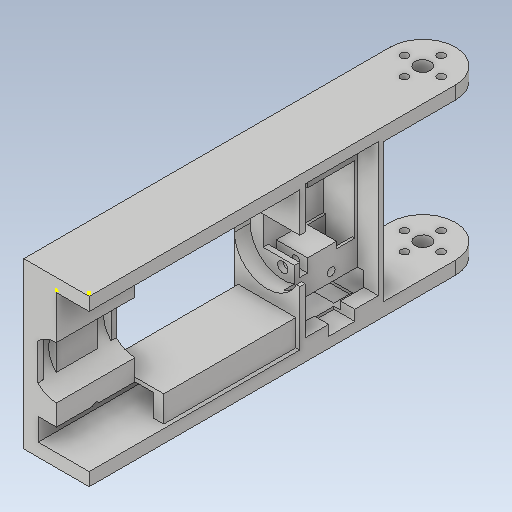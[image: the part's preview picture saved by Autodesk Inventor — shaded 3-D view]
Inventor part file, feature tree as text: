
AUTODESK INVENTOR PART (.ipt)
format: ipt  version: 2020.1 (Build 241239000, 239)  size: 703,488 bytes
history: native  units: mm
features: sketch x34, extrude x33, other x30, mirror x2
ambient origin geometry x8: Origin, YZ Plane, XZ Plane, XY Plane, X Axis, Y Axis, Z Axis, Center Point
bodies: Body1 (feature_tree), Body2 (feature_tree)
feature tree (99):
  other  "Sólido1"
  extrude  "Extrusión1"  Depth=25.0mm
  sketch  "Boceto2"  dims[d2=6.0mm d7=3.0mm]
  extrude  "Extrusión2"  Depth=3.0mm
  extrude  "Extrusión3"  Depth=5.0mm TaperAngle=0.0deg
  sketch  "Boceto5"  dims[d13=12.5mm d14=0.0mm d15=5.0mm d16=0.0mm]
  extrude  "Extrusión4"  Depth=33.0mm
  extrude  "Extrusión6"  Depth=5.0mm TaperAngle=0.0deg
  extrude  "Extrusión7"  Depth=7.0mm
  mirror  "Simetría1"
  mirror  "Simetría2"
  extrude  "Extrusión8"  Depth=2.0mm TaperAngle=0.0deg
  other  "Edición directa1"
  other  "Edición directa2"
  other  "Edición directa3"
  other  "Edición directa4"
  extrude  "Extrusión9"  Depth=2.0mm TaperAngle=0.0deg
  other  "Edición directa5"
  extrude  "Extrusión10"  Depth=0.5mm TaperAngle=0.0deg
  extrude  "Extrusión11"  TaperAngle=0.0deg  [1 undecoded]
  extrude  "Extrusión12"  Depth=28.0mm
  extrude  "Extrusión13"  Depth=4.0mm TaperAngle=0.0deg
  extrude  "Extrusión14"  Depth=8.0mm
  extrude  "Extrusión15"  Depth=3.0mm
  extrude  "Extrusión16"  Depth=18.0mm
  extrude  "Extrusión17"  Depth=3.0mm
  extrude  "Extrusión18"  Depth=7.5mm
  extrude  "Extrusión19"  Depth=7.0mm
  other  "Edición directa6"
  extrude  "Extrusión20"  Depth=3.5mm
  extrude  "Extrusión21"  Depth=27.0mm
  extrude  "Extrusión22"  Depth=0.5mm
  extrude  "Extrusión23"  Depth=25.0mm TaperAngle=0.0deg
  other  "Edición directa7"
  extrude  "Extrusión24"  Depth=5.0mm
  extrude  "Extrusión25"  TaperAngle=0.0deg  [1 undecoded]
  extrude  "Extrusión26"  Depth=2.0mm
  extrude  "Extrusión27"  TaperAngle=270.0deg  [1 undecoded]
  extrude  "Extrusión28"  Depth=2.0mm TaperAngle=0.0deg
  extrude  "Extrusión29"  Depth=9.0mm
  other  "Edición directa8"
  extrude  "Extrusión30"  Depth=5.5mm
  other  "Edición directa9"
  other  "Edición directa10"
  other  "Edición directa11"
  other  "Edición directa12"
  other  "Edición directa13"
  other  "Edición directa14"
  extrude  "Extrusion31"  Depth=3.0mm
  extrude  "Extrusion32"  Depth=3.5mm
  extrude  "Extrusion34"  Depth=2.0mm TaperAngle=0.0deg
  extrude  "Extrusion35"  Depth=5.0mm
  sketch  "Boceto1"  dims[d0=25.0mm d1=140.0mm]
  sketch  "Boceto3"  dims[d8=3.0mm d9=5.0mm d10=0.0mm]
  sketch  "Boceto4"  dims[d11=55.0mm d12=33.0mm]
  sketch  "Boceto6"  dims[d19=33.0mm d20=0.0mm d22=7.0mm]
  sketch  "Boceto7"  dims[d23=7.0mm d30=2.0mm d31=0.0mm]
  sketch  "Boceto10"  dims[d32=2.0mm d33=0.0mm d34=2.0mm d35=0.0mm]
  sketch  "Boceto11"  dims[d36=0.0mm d37=0.0mm d38=7.0mm d39=0.0mm d40=0.0mm d41=0.5mm]
  sketch  "Boceto15"  dims[d42=0.0mm d43=0.0mm d44=9.5mm d45=0.0mm d46=0.0mm d47=-3.0mm]
  sketch  "Boceto17"  dims[d48=25.0mm d49=28.0mm]
  sketch  "Boceto18"  dims[d50=25.0mm d51=0.0mm d60=0.0mm d61=0.0mm d62=4.0mm]
  sketch  "Boceto19"  dims[d63=5.5mm d64=8.0mm]
  sketch  "Boceto20"  dims[d65=5.5mm d66=3.0mm]
  sketch  "Boceto21"  dims[d67=18.0mm d68=24.5mm]
  sketch  "Boceto22"  dims[d69=5.5mm d70=3.0mm]
  sketch  "Boceto23"  dims[d71=5.0mm d72=7.5mm]
  sketch  "Boceto24"  dims[d73=20.0mm d74=0.0mm d75=7.0mm]
  sketch  "Boceto25"  dims[d76=0.5mm d77=3.5mm]
  sketch  "Boceto26"  dims[d78=3.0mm d81=27.0mm]
  sketch  "Boceto28"  dims[d82=0.5mm d84=0.5mm]
  sketch  "Boceto29"  dims[d85=3.0mm d86=25.0mm d87=0.0mm]
  sketch  "Boceto30"  dims[d88=7.0mm d89=5.0mm]
  sketch  "Boceto31"  dims[d90=5.0mm d91=0.0mm]
  sketch  "Boceto32"  dims[d92=13.5mm d93=0.0mm d94=2.0mm]
  sketch  "Boceto33"  dims[d95=18.0mm d96=270.0deg]
  sketch  "Boceto34"  dims[d97=1.0mm d98=2.0mm d99=0.0mm]
  sketch  "Boceto35"  dims[d100=9.5mm d101=9.0mm]
  sketch  "Boceto36"  dims[d102=3.0mm d104=5.5mm]
  sketch  "Boceto37"  dims[d105=4.25mm d106=3.0mm]
  sketch  "Sketch39"  dims[d107=23.0mm d108=0.0mm d109=3.5mm]
  sketch  "Sketch40"  dims[d110=3.5mm d111=2.0mm d112=0.0mm]
  sketch  "Sketch42"  dims[d113=14.0mm d114=5.0mm]
  sketch  "Sketch43"  dims[d115=5.0mm d116=2.0mm d117=0.0mm d118=4.0mm d119=4.0mm d120=9.0mm d121=0.0mm d122=15.0mm d123=15.0mm d124=3.0mm d125=3.0mm d126=12.5mm d127=0.0mm d128=3.5mm d129=2.0mm d130=0.0mm d131=0.0mm d132=0.0mm d133=-15.0mm d134=65.0mm d135=0.0mm d137=65.0mm d138=0.0mm d139=15.0mm d140=0.0mm d141=15.0mm d142=0.0mm d143=0.0mm d144=0.0mm d145=-6.0mm d146=10.0mm d147=0.0mm d148=9.0mm d149=0.0mm d150=9.0mm d151=3.0mm d152=17.0mm d153=0.0mm d154=3.5mm d155=2.0mm d156=0.0mm d157=1.0mm d158=7.0mm d159=90.0deg d160=10.0mm d161=80.0mm d162=0.0mm d163=2.5mm d164=0.0mm d166=6.0mm d167=0.0mm d168=0.0mm d169=0.0mm d170=-1.0mm d171=1.0mm d172=0.0mm d173=0.0mm d174=0.0mm d175=1.3mm d176=0.0mm d177=-0.7mm d178=0.0mm d179=0.0mm d180=2.0mm d181=0.0mm d182=0.0mm d183=0.0mm d184=0.5mm d185=0.0mm d186=0.0mm d187=1.8mm d188=0.0mm d189=0.0mm d190=1.0mm d191=0.0mm d192=0.0mm d193=1.0mm d194=10.0mm d195=11.0mm d196=22.0mm d197=10.0mm d198=0.0mm d199=10.0mm d203=0.0mm d204=0.0mm d210=8.5mm d211=7.0mm d212=14.0mm d213=8.5mm d214=11.0mm d215=7.0mm d216=12.0mm d217=7.0mm d218=10.0mm d219=0.0mm d220=15.0mm d221=7.0mm d222=11.0mm d223=10.0mm d224=17.0mm d225=10.0mm d226=0.0mm]
  other  "Desplazar1"
  other  "Desplazar2"
  other  "Desplazar3"
  other  "Desplazar4"
  other  "Desplazar5"
  other  "Desplazar6"
  other  "Desplazar7"
  other  "Desplazar8"
  other  "Desplazar9"
  other  "Desplazar10"
  other  "Desplazar11"
  other  "Desplazar12"
  other  "Desplazar13"
  other  "Desplazar14"
  other  "Desplazar15"
note: 3 required parameter values undecoded (feature->parameter linkage not recoverable at this tier; creation-order binding heuristic only, values carry confidence <= 0.55)
